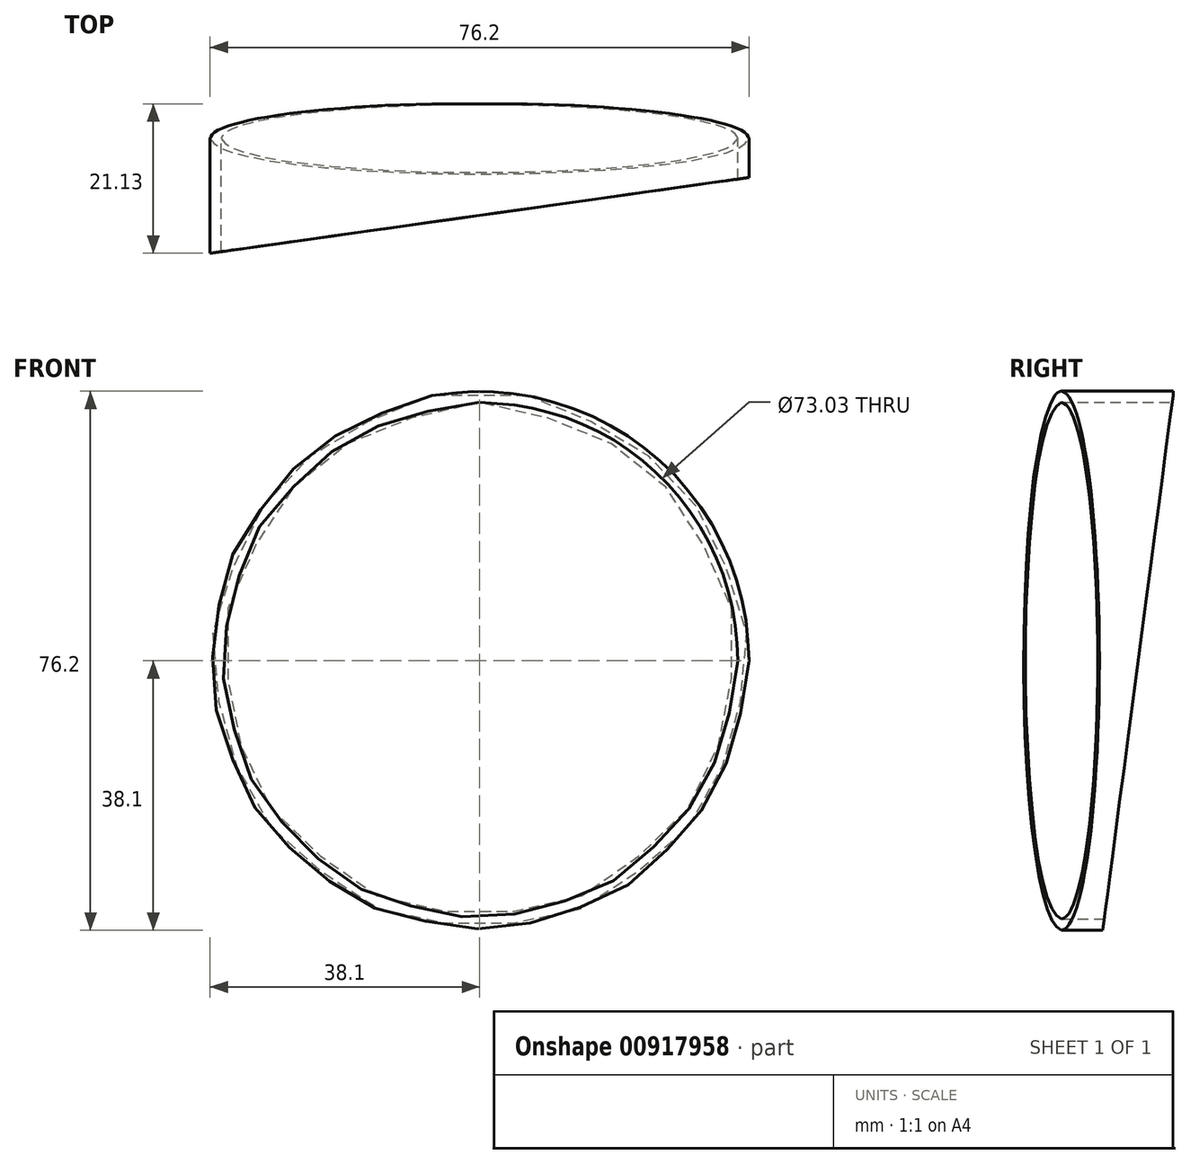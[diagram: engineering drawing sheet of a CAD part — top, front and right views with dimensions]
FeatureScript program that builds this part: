
annotation { "Feature Type Name" : "Feature", "Feature Type Description" : "" }
export const myFeature = defineFeature(function(context is Context, id is Id, definition is map)
    precondition{}
    {
        {
            var Q0;
            Q0=qCreatedBy(makeId("Front.planeOp"),FACE);
            var sketch = newSketch(context, id + "F0", { "sketchPlane" : qUnion([Q0])});
            skCircle(sketch, "E0", {"center": v(0, 38.1) * mm, "radius": 38.1 * mm});
            skCircle(sketch, "E1", {"center": v(0, 38.1) * mm, "radius": 36.51 * mm});
            skPoint(sketch, "E2", {"position": v(0, 0) * mm});
            skSolve(sketch);
        }
        {
            var Q0;
            Q0 = qSketchRegion(id + "F0", true);
            extrude(context, id + "F1", {"entities" : qUnion([Q0]), "endBound" : BoundingType.SYMMETRIC, "depth" : 25.4 * mm, "offsetDistance" : 25.4 * mm});
        }
        {
            var Q0;
            Q0=qCreatedBy(makeId("Right.planeOp"),FACE);
            var sketch = newSketch(context, id + "F2", { "sketchPlane" : qUnion([Q0])});
            skLineSegment(sketch, "E3", {"start": v(-17.2, -61.29) * mm, "end": v(-17.2, 43.26) * mm});
            skSolve(sketch);
        }
        {
            var Q0;
            Q0=qCreatedBy(makeId("Right.planeOp"),FACE);
            var Q1;
            Q1=sQuery(id+"F2.wireOp",EDGE,"E3");
            cPlane(context, id + "F3", {"entities" : qUnion([Q0, Q1]), "cplaneType" : CPlaneType.LINE_ANGLE, "offset" : 25.4 * mm, "angle" : 8 * degree, "width" : 152.4 * mm, "height" : 152.4 * mm});
        }
        {
            var Q0;
            Q0=qCreatedBy(makeId("Right.planeOp"),FACE);
            var sketch = newSketch(context, id + "F4", { "sketchPlane" : qUnion([Q0])});
            skLineSegment(sketch, "E4", {"start": v(12.78, 76.2) * mm, "end": v(1.59, -8.82) * mm});
            skLineSegment(sketch, "E5", {"start": v(12.78, 76.2) * mm, "end": v(12.78, -8.82) * mm});
            skLineSegment(sketch, "E6", {"start": v(12.78, -8.82) * mm, "end": v(1.59, -8.82) * mm});
            skSolve(sketch);
        }
        {
            var Q0;
            Q0 = qSketchRegion(id + "F4", true);
            extrude(context, id + "F5", {"entities" : qUnion([Q0]), "operationType" : NewBodyOperationType.REMOVE, "endBound" : BoundingType.SYMMETRIC, "oppositeDirection" : true, "depth" : 76.2 * mm, "offsetDistance" : 25.4 * mm});
        }
        {
            var Q0;
            Q0=qCreatedBy(id+"F3.planeOp",FACE);
            cPlane(context, id + "F6", {"entities" : qUnion([Q0]), "cplaneType" : CPlaneType.OFFSET, "offset" : 4.57 * mm, "oppositeDirection" : true, "width" : 152.4 * mm, "height" : 152.4 * mm});
        }
        {
            var Q0;
            Q0=qCreatedBy(id+"F6.planeOp",FACE);
            var sketch = newSketch(context, id + "F7", { "sketchPlane" : qUnion([Q0])});
            skLineSegment(sketch, "E7", {"start": v(3.05, 76.52) * mm, "end": v(3.05, -2.23) * mm});
            skLineSegment(sketch, "E8", {"start": v(3.05, -2.23) * mm, "end": v(31.61, -2.23) * mm});
            skLineSegment(sketch, "E9", {"start": v(31.61, -2.23) * mm, "end": v(31.61, 76.02) * mm});
            skLineSegment(sketch, "E10", {"start": v(31.61, 76.02) * mm, "end": v(3.05, 76.52) * mm});
            skSolve(sketch);
        }
        {
            var Q0;
            Q0 = qSketchRegion(id + "F7", true);
            extrude(context, id + "F8", {"entities" : qUnion([Q0]), "operationType" : NewBodyOperationType.REMOVE, "endBound" : BoundingType.SYMMETRIC, "oppositeDirection" : true, "depth" : 101.6 * mm, "offsetDistance" : 25.4 * mm});
        }
    });
